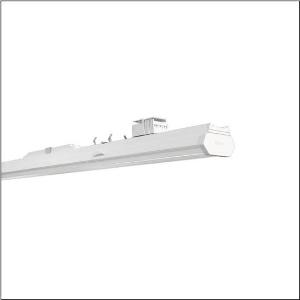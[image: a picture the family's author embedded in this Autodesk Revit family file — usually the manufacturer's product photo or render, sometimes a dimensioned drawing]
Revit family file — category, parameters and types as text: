
# Revit family: licross_r__11_protected_mo_51td12dn495g3s_4e23
name_source: partatom
category: Lighting Fixtures
units: mm (PartAtom-declared; Revit-internal decimal feet)

## family parameters
Cut with Voids When Loaded = No
Host = Face
Light Source = No
Part Type = Normal
Room Calculation Point = No
Round Connector Dimension = Use Diameter
Shared = No

## types (1)
- --- (1 x LED, 980 lm, 6.8 W, 4000K)
    Apparent Load = 7 VA
    CIE Flux Codes = 73 92 98 99 100
    Color Rendering = 80
    Color Temperature = 4000K
    Default Elevation = 1800 mm
    Description = Licross® 11 Protected MO, luminaire insert, of sheet steel, galvanised, coil coated, white, length: 1.500mm, width: 90mm, height: 101mm, LED rated luminous flux: 9.980lm, light colour: 840, control gear: DALI 2 (for two DALI lines), with plug, 6-pole, with phase selection, for trunking rail, 14-core, mains connection: 220..240V, AC, 50/60Hz, rated input power: 61W, for trunking rail, 14-core, halogen-free wiring, for emergency light function, converter,control gear: single battery element, battery: LiFePO4, 9Ah, primary light control with lens, of plastic, primary optical cover: cover, of PMMA, light emission: direct distribution, primary light characteristic: symmetric, protection rating (complete): IP54, insulation class (complete): insulation class I (protective earthing), certification: CE, UKCA, protection symbol: D if used in an environment with non-conductive dust loads with corresponding accessories, impact resistance: IK06, permissible ambient temperature for indoor applications: +5..+35°C, standard: EN 60598-2-22, LABS conformity tested according to VDMA 24364:2018-05, reducing of maximum allowable ambient temperature of 5°C with ceiling mounting, corresponds to IFS (International Featured Standards) requirements for safety and quality in the food industry, packaging unit: 1 piece
    Height = 92 mm
    Lamp = 1 x LED
    Lamp Light Flux = 980 lm
    Lamp Power = 6.8 W
    Lamp count = 1
    Length = 1500 mm
    Luminous efficacy = 144 lm/W
    Manufacturer = Siteco
    ModVariant = No
    Model = 51TD12DN495G3S
    Mounting Place = Ceiling
    Mounting Type = Pendant
    Number of Poles = 1
    OnlyDefault = Yes
    Power Factor = 1
    Product Name = Licross® 11 Protected MO
    Product group = luminaire insert
    ProductGroupID = 901
    Protection Class = Protection class I
    Protection Degree = IP 54
    RLX_Detail_Level = 1
    RLX_Emergency_Light_Flux = 0 lm
    RLX_Emergency_Type = 0
    RLX_Emergency_Type_DB = No
    RlxData = <blob elided: 24733 chars, md5=1267d2d5>
    Socket = socket
    Standby Power = 0 W
    System Light Flux = 980 lm
    System Power = 7 W
    Type Comments = : emergency light operation: 3 h
    Type Image = l_1256145.jpg
    URL = http://relux.com
    VarID = @adj_059533
    Voltage = 0 V
    Weight = 0.00 kg
    Width = 88 mm

## geometry (parser evidence)
native form markers: Blend x4, Sweep x11
no freeform markers — native parametric forms only
